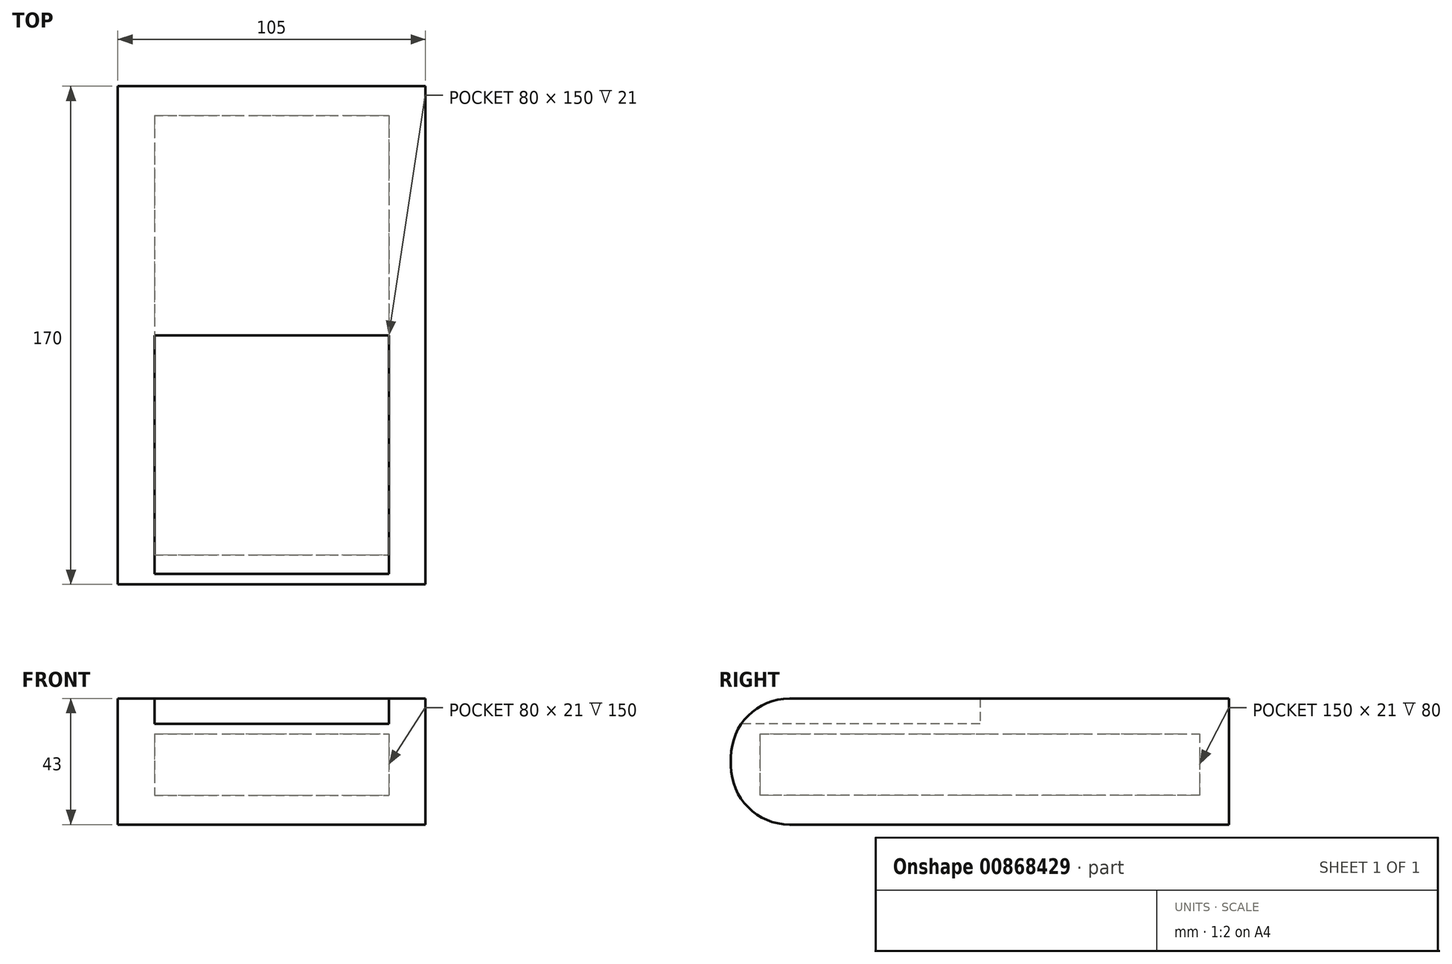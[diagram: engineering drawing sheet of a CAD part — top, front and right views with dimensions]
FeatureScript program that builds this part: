
annotation { "Feature Type Name" : "Feature", "Feature Type Description" : "" }
export const myFeature = defineFeature(function(context is Context, id is Id, definition is map)
    precondition{}
    {
        {
            var Q0;
            Q0=qCreatedBy(makeId("Right.planeOp"),FACE);
            var sketch = newSketch(context, id + "F0", { "sketchPlane" : qUnion([Q0])});
            skLineSegment(sketch, "E0.bottom", {"start": v(-85, 1.5) * mm, "end": v(85, 1.5) * mm});
            skLineSegment(sketch, "E0.top", {"start": v(-85, -1.5) * mm, "end": v(85, -1.5) * mm});
            skLineSegment(sketch, "E0.left", {"start": v(-85, 1.5) * mm, "end": v(-85, -1.5) * mm});
            skLineSegment(sketch, "E0.right", {"start": v(85, 1.5) * mm, "end": v(85, -1.5) * mm});
            skPoint(sketch, "E0.middle", {"position": v(0, 0) * mm});
            skLineSegment(sketch, "E1", {"start": v(-85, 1.5) * mm, "end": v(-85, 1.5) * mm});
            skLineSegment(sketch, "E2", {"start": v(-85, -1.5) * mm, "end": v(-85, -1.5) * mm});
            skLineSegment(sketch, "E3", {"start": v(85, 1.5) * mm, "end": v(85, 21.5) * mm});
            skLineSegment(sketch, "E4", {"start": v(85, 21.5) * mm, "end": v(-65, 21.5) * mm});
            skLineSegment(sketch, "E5", {"start": v(85, -1.5) * mm, "end": v(85, -21.5) * mm});
            skLineSegment(sketch, "E6", {"start": v(85, -21.5) * mm, "end": v(-65, -21.5) * mm});
            skPoint(sketch, "E7.visualSharp", {"position": v(-85, 21.5) * mm});
            skArc(sketch, "E7.filletArc", {"start": v(-65, 21.5) * mm, "mid": v(-79.14, 15.64) * mm, "end": v(-85, 1.5) * mm});
            skPoint(sketch, "E8.visualSharp", {"position": v(-85, -21.5) * mm});
            skArc(sketch, "E8.filletArc", {"start": v(-85, -1.5) * mm, "mid": v(-79.14, -15.64) * mm, "end": v(-65, -21.5) * mm});
            skSolve(sketch);
        }
        {
            var Q0;
            Q0=makeQuery(id+"F0.imprint","IMPRINT",FACE,{"disambiguationData":[TD([[makeQuery(id+"F0.imprint","IMPRINT",EDGE,{"derivedFrom":sQuery(id+"F0.wireOp",EDGE,"E0.bottom")}),1.0]])]});
            var Q1;
            Q1=makeQuery(id+"F0.imprint","IMPRINT",FACE,{"disambiguationData":[TD([[makeQuery(id+"F0.imprint","IMPRINT",EDGE,{"derivedFrom":sQuery(id+"F0.wireOp",EDGE,"E0.top")}),-1.0]])]});
            var Q2;
            Q2=makeQuery(id+"F0.imprint","IMPRINT",FACE,{"disambiguationData":[TD([[makeQuery(id+"F0.imprint","IMPRINT",EDGE,{"derivedFrom":sQuery(id+"F0.wireOp",EDGE,"E0.bottom")}),-1.0]])]});
            extrude(context, id + "F1", {"entities" : qUnion([Q0, Q1, Q2]), "endBound" : BoundingType.SYMMETRIC, "depth" : 105 * mm, "offsetDistance" : 25 * mm});
        }
        {
            var Q0;
            Q0=qCreatedBy(makeId("Right.planeOp"),FACE);
            var sketch = newSketch(context, id + "F2", { "sketchPlane" : qUnion([Q0])});
            skLineSegment(sketch, "E9", {"start": v(0, 0) * mm, "end": v(0, -1.5) * mm});
            skLineSegment(sketch, "E10", {"start": v(75, -11.5) * mm, "end": v(-75, -11.5) * mm});
            skLineSegment(sketch, "E11", {"start": v(-75, -11.5) * mm, "end": v(-75, -1.5) * mm});
            skLineSegment(sketch, "E12", {"start": v(-75, -1.5) * mm, "end": v(-75, 0) * mm});
            skLineSegment(sketch, "E13", {"start": v(-75, 0) * mm, "end": v(-75, 1.5) * mm});
            skLineSegment(sketch, "E14", {"start": v(-75, 1.5) * mm, "end": v(-75, 9.5) * mm});
            skLineSegment(sketch, "E15", {"start": v(-75, 9.5) * mm, "end": v(75, 9.5) * mm});
            skLineSegment(sketch, "E16", {"start": v(75, 9.5) * mm, "end": v(75, -11.5) * mm});
            skLineSegment(sketch, "E17", {"start": v(0, 22.92) * mm, "end": v(0, 12.92) * mm});
            skLineSegment(sketch, "E18", {"start": v(0, 12.92) * mm, "end": v(-84.38, 12.92) * mm});
            skPoint(sketch, "E19.orphan", {"position": v(85, 9.5) * mm});
            skPoint(sketch, "E20.start.orphan", {"position": v(85, -1.5) * mm});
            skLineSegment(sketch, "E21", {"start": v(0, 22.92) * mm, "end": v(-87.27, 22.92) * mm});
            skLineSegment(sketch, "E22", {"start": v(-87.27, 22.92) * mm, "end": v(-84.38, 12.92) * mm});
            skSolve(sketch);
        }
        {
            var Q0;
            Q0=makeQuery(id+"F2.imprint","IMPRINT",FACE,{"disambiguationData":[TD([[makeQuery(id+"F2.imprint","IMPRINT",EDGE,{"derivedFrom":sQuery(id+"F2.wireOp",EDGE,"E17")}),-1.0]])]});
            extrude(context, id + "F3", {"entities" : qUnion([Q0]), "operationType" : NewBodyOperationType.REMOVE, "endBound" : BoundingType.SYMMETRIC, "depth" : 80 * mm, "offsetDistance" : 25 * mm});
        }
        {
            var Q0;
            Q0=qSketchRegion(id+"F2",true);
            extrude(context, id + "F4", {"entities" : qUnion([Q0]), "operationType" : NewBodyOperationType.REMOVE, "endBound" : BoundingType.SYMMETRIC, "oppositeDirection" : true, "depth" : 80 * mm, "offsetDistance" : 25 * mm});
        }
    });
